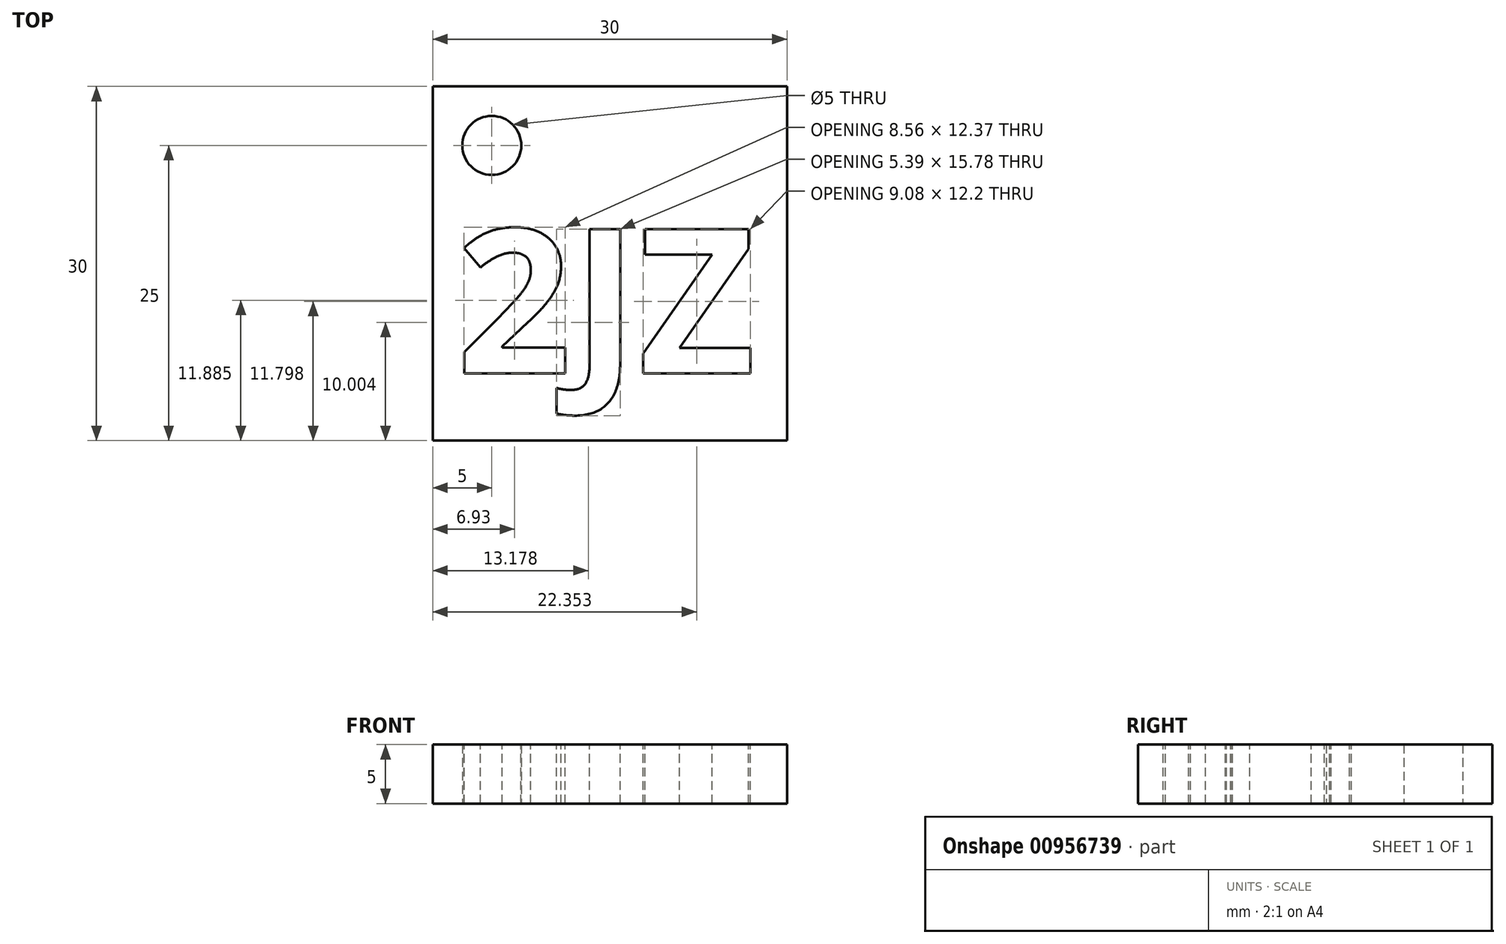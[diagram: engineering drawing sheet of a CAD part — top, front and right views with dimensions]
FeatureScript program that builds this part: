
annotation { "Feature Type Name" : "Feature", "Feature Type Description" : "" }
export const myFeature = defineFeature(function(context is Context, id is Id, definition is map)
    precondition{}
    {
        {
            var Q0;
            Q0=qCreatedBy(makeId("Top.planeOp"),FACE);
            var sketch = newSketch(context, id + "F0", { "sketchPlane" : qUnion([Q0])});
            skLineSegment(sketch, "E0.bottom", {"start": v(0, 0) * mm, "end": v(30, 0) * mm});
            skLineSegment(sketch, "E0.top", {"start": v(0, -30) * mm, "end": v(30, -30) * mm});
            skLineSegment(sketch, "E0.left", {"start": v(0, 0) * mm, "end": v(0, -30) * mm});
            skLineSegment(sketch, "E0.right", {"start": v(30, 0) * mm, "end": v(30, -30) * mm});
            skCircle(sketch, "E1", {"center": v(5, -5) * mm, "radius": 2.5 * mm});
            skSolve(sketch);
        }
        {
            var Q0;
            Q0=makeQuery(id+"F0.imprint","IMPRINT",FACE,{"disambiguationData":[TD([[makeQuery(id+"F0.imprint","IMPRINT",EDGE,{"derivedFrom":sQuery(id+"F0.wireOp",EDGE,"E0.bottom")}),-1.0]])]});
            extrude(context, id + "F1", {"entities" : qUnion([Q0]), "depth" : 5 * mm, "offsetDistance" : 25 * mm});
        }
        {
            var Q0;
            Q0=makeQuery(id+"F1.opExtrude","CAP_FACE",FACE,{"disambiguationData":[OSD([sQuery(id+"F0.wireOp",EDGE,"E0.bottom"),sQuery(id+"F0.wireOp",EDGE,"E0.top"),sQuery(id+"F0.wireOp",EDGE,"E0.left"),sQuery(id+"F0.wireOp",EDGE,"E0.right"),sQuery(id+"F0.wireOp",EDGE,"E1")])],"isStart":false});
            var sketch = newSketch(context, id + "F2", { "sketchPlane" : qUnion([Q0])});
            skText(sketch, "E2", { "text": "2JZ", "fontName": "OpenSans-Bold.ttf"});
            const initialGuessF2  = {"E2": [0.002, -0.0243, 1, 0, 0.0123]};
            skSetInitialGuess(sketch, initialGuessF2);
            skSolve(sketch);
        }
        {
            var Q0;
            Q0 = qSketchRegion(id + "F2", true);
            extrude(context, id + "F3", {"entities" : qUnion([Q0]), "operationType" : NewBodyOperationType.REMOVE, "endBound" : BoundingType.THROUGH_ALL, "oppositeDirection" : true, "depth" : 25 * mm, "offsetDistance" : 25 * mm});
        }
    });
